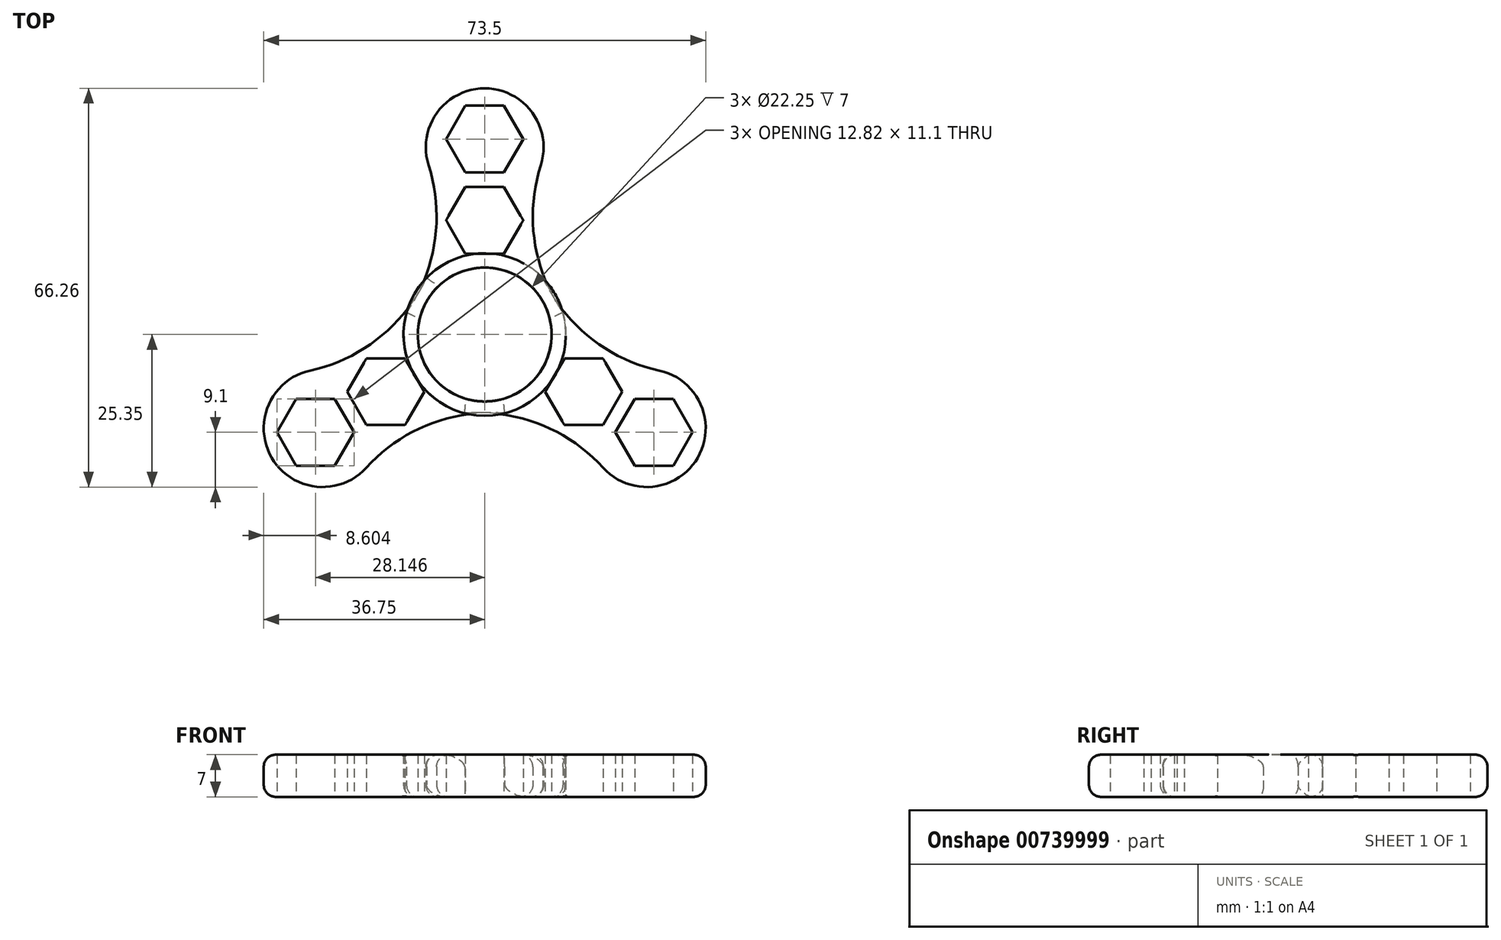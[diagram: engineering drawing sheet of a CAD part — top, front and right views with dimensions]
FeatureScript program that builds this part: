
annotation { "Feature Type Name" : "Feature", "Feature Type Description" : "" }
export const myFeature = defineFeature(function(context is Context, id is Id, definition is map)
    precondition{}
    {
        {
            var Q0;
            Q0=qCreatedBy(makeId("Top.planeOp"),FACE);
            var sketch = newSketch(context, id + "F0", { "sketchPlane" : qUnion([Q0])});
            skCircle(sketch, "E0", {"center": v(0, 0) * mm, "radius": 11.12 * mm});
            skCircle(sketch, "E1.cCircle", {"center": v(0, 19) * mm, "radius": 5.55 * mm, "construction": true});
            skLineSegment(sketch, "E1.0", {"start": v(3.2, 13.45) * mm, "end": v(-3.2, 13.45) * mm});
            skLineSegment(sketch, "E1.1", {"start": v(-3.2, 13.45) * mm, "end": v(-6.4, 19) * mm});
            skLineSegment(sketch, "E1.2", {"start": v(-6.4, 19) * mm, "end": v(-3.2, 24.55) * mm});
            skLineSegment(sketch, "E1.3", {"start": v(-3.2, 24.55) * mm, "end": v(3.2, 24.55) * mm});
            skLineSegment(sketch, "E1.4", {"start": v(3.2, 24.55) * mm, "end": v(6.4, 19) * mm});
            skLineSegment(sketch, "E1.5", {"start": v(6.4, 19) * mm, "end": v(3.2, 13.45) * mm});
            skPoint(sketch, "E1.0.midPoint", {"position": v(0, 13.45) * mm});
            skArc(sketch, "E2", {"start": v(-10.12, 8.94) * mm, "mid": v(0, -13.5) * mm, "end": v(10.12, 8.94) * mm});
            skArc(sketch, "E3", {"start": v(-4.45, 22.4) * mm, "mid": v(-4.43, 22.39) * mm, "end": v(-4.4, 22.38) * mm});
            skArc(sketch, "E4", {"start": v(-13, 3.66) * mm, "mid": v(-8.3, 15.47) * mm, "end": v(-9.33, 28.14) * mm});
            skArc(sketch, "E5", {"start": v(9.33, 28.14) * mm, "mid": v(8.3, 15.47) * mm, "end": v(13, 3.66) * mm});
            skPoint(sketch, "E6", {"position": v(0, 24.55) * mm});
            skCircle(sketch, "E7.cCircle", {"center": v(0, 32.5) * mm, "radius": 5.55 * mm, "construction": true});
            skLineSegment(sketch, "E7.0", {"start": v(3.2, 26.95) * mm, "end": v(-3.2, 26.95) * mm});
            skLineSegment(sketch, "E7.1", {"start": v(-3.2, 26.95) * mm, "end": v(-6.4, 32.5) * mm});
            skLineSegment(sketch, "E7.2", {"start": v(-6.4, 32.5) * mm, "end": v(-3.2, 38.05) * mm});
            skLineSegment(sketch, "E7.3", {"start": v(-3.2, 38.05) * mm, "end": v(3.2, 38.05) * mm});
            skLineSegment(sketch, "E7.4", {"start": v(3.2, 38.05) * mm, "end": v(6.4, 32.5) * mm});
            skLineSegment(sketch, "E7.5", {"start": v(6.4, 32.5) * mm, "end": v(3.2, 26.95) * mm});
            skPoint(sketch, "E7.0.midPoint", {"position": v(0, 26.95) * mm});
            skArc(sketch, "E8.trimOffspring", {"start": v(4.4, 22.38) * mm, "mid": v(4.43, 22.39) * mm, "end": v(4.45, 22.4) * mm});
            skArc(sketch, "E9.trimOffspring", {"start": v(9.33, 28.14) * mm, "mid": v(0, 40.91) * mm, "end": v(-9.33, 28.14) * mm});
            skSolve(sketch);
        }
        {
            var Q0;
            Q0=makeQuery(id+"F0.imprint","IMPRINT",FACE,{"disambiguationData":[TD([[makeQuery(id+"F0.imprint","IMPRINT",EDGE,{"derivedFrom":sQuery(id+"F0.wireOp",EDGE,"E0")}),-1.0]])]});
            extrude(context, id + "F1", {"entities" : qUnion([Q0]), "depth" : 7 * mm, "offsetDistance" : 25 * mm});
        }
        {
            var Q0;
            Q0=makeQuery(id+"F1.opExtrude","SWEPT_BODY",BODY,{"disambiguationData":[OSD([sQuery(id+"F0.wireOp",EDGE,"E0"),sQuery(id+"F0.wireOp",EDGE,"MDsEToRO-sDo8-RBbG-tWF8-SreFTiSiscwj"),sQuery(id+"F0.wireOp",EDGE,"8695b1e1-9288-4cb8-b92b-e351c22f4dc8.0"),sQuery(id+"F0.wireOp",EDGE,"8695b1e1-9288-4cb8-b92b-e351c22f4dc8.1"),sQuery(id+"F0.wireOp",EDGE,"8695b1e1-9288-4cb8-b92b-e351c22f4dc8.2"),sQuery(id+"F0.wireOp",EDGE,"8695b1e1-9288-4cb8-b92b-e351c22f4dc8.3"),sQuery(id+"F0.wireOp",EDGE,"8695b1e1-9288-4cb8-b92b-e351c22f4dc8.4"),sQuery(id+"F0.wireOp",EDGE,"8695b1e1-9288-4cb8-b92b-e351c22f4dc8.5"),sQuery(id+"F0.wireOp",EDGE,"7e2a876e-0c3f-4791-89cb-893942d8e054.0"),sQuery(id+"F0.wireOp",EDGE,"7e2a876e-0c3f-4791-89cb-893942d8e054.1"),sQuery(id+"F0.wireOp",EDGE,"7e2a876e-0c3f-4791-89cb-893942d8e054.2"),sQuery(id+"F0.wireOp",EDGE,"7e2a876e-0c3f-4791-89cb-893942d8e054.3"),sQuery(id+"F0.wireOp",EDGE,"7e2a876e-0c3f-4791-89cb-893942d8e054.4"),sQuery(id+"F0.wireOp",EDGE,"7e2a876e-0c3f-4791-89cb-893942d8e054.5"),sQuery(id+"F0.wireOp",EDGE,"6b78wPmF-SaVM-O4K7-W1F7-SZ1nQxVpJnyN"),sQuery(id+"F0.wireOp",EDGE,"JJtaek0i-86pv-hUof-ZRD0-zzxheRi3Trb6"),sQuery(id+"F0.wireOp",EDGE,"4f531992-08b8-4dfa-bfd4-d564cd5343f0.trimOffspring")])]});
            var Q1;
            Q1=makeQuery(id+"F1.opExtrude","CAP_EDGE",EDGE,{"disambiguationData":[OSD([sQuery(id+"F0.wireOp",EDGE,"E0")])],"isStart":false});
            circularPattern(context, id + "F2", {"entities" : qUnion([Q0]), "axis" : qUnion([Q1]), "angle" : 360 * degree, "instanceCount" : 3, "equalSpace" : true});
        }
        {
            var Q0;
            Q0=makeQuery(id+"F2.opPattern","COPY",EDGE,{"derivedFrom":makeQuery(id+"F1.opExtrude","CAP_EDGE",EDGE,{"disambiguationData":[OSD([sQuery(id+"F0.wireOp",EDGE,"E4")])],"isStart":false}),"instanceName":"2"});
            var Q1;
            Q1=makeQuery(id+"F2.opPattern","COPY",EDGE,{"derivedFrom":makeQuery(id+"F1.opExtrude","CAP_EDGE",EDGE,{"disambiguationData":[OSD([sQuery(id+"F0.wireOp",EDGE,"E9.trimOffspring")])],"isStart":true}),"instanceName":"2"});
            var Q2;
            Q2=makeQuery(id+"F2.opPattern","COPY",EDGE,{"derivedFrom":makeQuery(id+"F1.opExtrude","CAP_EDGE",EDGE,{"disambiguationData":[OSD([sQuery(id+"F0.wireOp",EDGE,"E9.trimOffspring")])],"isStart":true}),"instanceName":"1"});
            var Q3;
            Q3=makeQuery(id+"F2.opPattern","COPY",EDGE,{"derivedFrom":makeQuery(id+"F1.opExtrude","CAP_EDGE",EDGE,{"disambiguationData":[OSD([sQuery(id+"F0.wireOp",EDGE,"E9.trimOffspring")])],"isStart":false}),"instanceName":"1"});
            var Q4;
            Q4=makeQuery(id+"F2.opPattern","COPY",EDGE,{"derivedFrom":makeQuery(id+"F1.opExtrude","CAP_EDGE",EDGE,{"disambiguationData":[OSD([sQuery(id+"F0.wireOp",EDGE,"E2")])],"isStart":false}),"instanceName":"1"});
            var Q5;
            Q5=makeQuery(id+"F2.opPattern","COPY",EDGE,{"derivedFrom":makeQuery(id+"F1.opExtrude","CAP_EDGE",EDGE,{"disambiguationData":[OSD([sQuery(id+"F0.wireOp",EDGE,"E4")])],"isStart":true}),"instanceName":"2"});
            var Q6;
            Q6=makeQuery(id+"F1.opExtrude","CAP_EDGE",EDGE,{"disambiguationData":[OSD([sQuery(id+"F0.wireOp",EDGE,"E5")])],"isStart":true});
            var Q7;
            Q7=makeQuery(id+"F1.opExtrude","CAP_EDGE",EDGE,{"disambiguationData":[OSD([sQuery(id+"F0.wireOp",EDGE,"E9.trimOffspring")])],"isStart":true});
            var Q8;
            Q8=makeQuery(id+"F1.opExtrude","CAP_EDGE",EDGE,{"disambiguationData":[OSD([sQuery(id+"F0.wireOp",EDGE,"E4")])],"isStart":true});
            var Q9;
            Q9=makeQuery(id+"F2.opPattern","COPY",EDGE,{"derivedFrom":makeQuery(id+"F1.opExtrude","CAP_EDGE",EDGE,{"disambiguationData":[OSD([sQuery(id+"F0.wireOp",EDGE,"E5")])],"isStart":true}),"instanceName":"1"});
            var Q10;
            Q10=makeQuery(id+"F2.opPattern","COPY",EDGE,{"derivedFrom":makeQuery(id+"F1.opExtrude","CAP_EDGE",EDGE,{"disambiguationData":[OSD([sQuery(id+"F0.wireOp",EDGE,"E4")])],"isStart":true}),"instanceName":"1"});
            var Q11;
            Q11=makeQuery(id+"F2.opPattern","COPY",EDGE,{"derivedFrom":makeQuery(id+"F1.opExtrude","CAP_EDGE",EDGE,{"disambiguationData":[OSD([sQuery(id+"F0.wireOp",EDGE,"E5")])],"isStart":true}),"instanceName":"2"});
            var Q12;
            Q12=makeQuery(id+"F2.opPattern","COPY",EDGE,{"derivedFrom":makeQuery(id+"F1.opExtrude","CAP_EDGE",EDGE,{"disambiguationData":[OSD([sQuery(id+"F0.wireOp",EDGE,"E9.trimOffspring")])],"isStart":false}),"instanceName":"2"});
            var Q13;
            Q13=makeQuery(id+"F2.opPattern","COPY",EDGE,{"derivedFrom":makeQuery(id+"F1.opExtrude","CAP_EDGE",EDGE,{"disambiguationData":[OSD([sQuery(id+"F0.wireOp",EDGE,"E4")])],"isStart":false}),"instanceName":"1"});
            var Q14;
            Q14=makeQuery(id+"F2.opPattern","COPY",EDGE,{"derivedFrom":makeQuery(id+"F1.opExtrude","CAP_EDGE",EDGE,{"disambiguationData":[OSD([sQuery(id+"F0.wireOp",EDGE,"E5")])],"isStart":false}),"instanceName":"1"});
            var Q15;
            Q15=makeQuery(id+"F1.opExtrude","CAP_EDGE",EDGE,{"disambiguationData":[OSD([sQuery(id+"F0.wireOp",EDGE,"E4")])],"isStart":false});
            var Q16;
            Q16=makeQuery(id+"F2.opPattern","COPY",EDGE,{"derivedFrom":makeQuery(id+"F1.opExtrude","CAP_EDGE",EDGE,{"disambiguationData":[OSD([sQuery(id+"F0.wireOp",EDGE,"E2")])],"isStart":true}),"instanceName":"2"});
            var Q17;
            Q17=makeQuery(id+"F1.opExtrude","CAP_EDGE",EDGE,{"disambiguationData":[OSD([sQuery(id+"F0.wireOp",EDGE,"E2")])],"isStart":true});
            var Q18;
            Q18=makeQuery(id+"F1.opExtrude","CAP_EDGE",EDGE,{"disambiguationData":[OSD([sQuery(id+"F0.wireOp",EDGE,"E5")])],"isStart":false});
            var Q19;
            Q19=makeQuery(id+"F1.opExtrude","CAP_EDGE",EDGE,{"disambiguationData":[OSD([sQuery(id+"F0.wireOp",EDGE,"E9.trimOffspring")])],"isStart":false});
            var Q20;
            Q20=makeQuery(id+"F2.opPattern","COPY",EDGE,{"derivedFrom":makeQuery(id+"F1.opExtrude","CAP_EDGE",EDGE,{"disambiguationData":[OSD([sQuery(id+"F0.wireOp",EDGE,"E5")])],"isStart":false}),"instanceName":"2"});
            fillet(context, id + "F3", {"entities" : qUnion([Q0, Q1, Q2, Q3, Q4, Q5, Q6, Q7, Q8, Q9, Q10, Q11, Q12, Q13, Q14, Q15, Q16, Q17, Q18, Q19, Q20]), "radius" : 2 * mm, "tangentPropagation" : true, "allowEdgeOverflow" : false});
        }
    });
